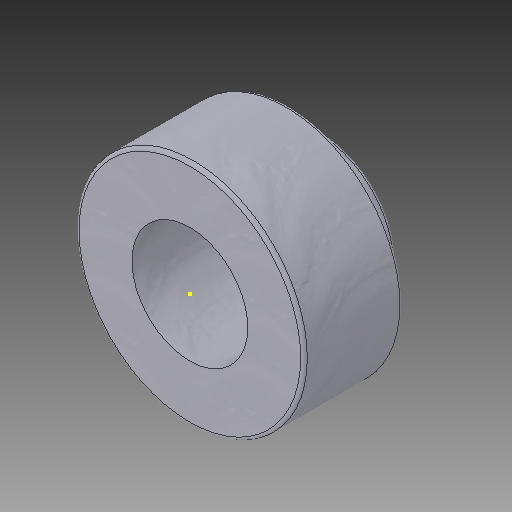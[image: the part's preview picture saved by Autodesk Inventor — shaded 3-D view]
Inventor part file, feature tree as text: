
AUTODESK INVENTOR PART (.ipt)
format: ipt  version: 2019 (Build 230136000, 136)  size: 205,824 bytes
history: native  units: in
note: dims shown in document units (in); Inventor stores cm internally (conversion verified against a paired STEP export)
features: sketch x6, other x3
ambient origin geometry x8: Origin, YZ Plane, XZ Plane, XY Plane, X Axis, Y Axis, Z Axis, Center Point
bodies: Solid1 (feature_tree)
feature tree (9):
  other  "project flange bearing part2.ipt"
  other  "Solid1::project flange bearing part2.ipt"
  other  "TaggingFeature1"
  sketch  "Sketch1"  dims[d0=0.3937in]
  sketch  "Sketch2"
  sketch  "Sketch3"
  sketch  "Sketch4"
  sketch  "Sketch5"
  sketch  "Sketch6"
